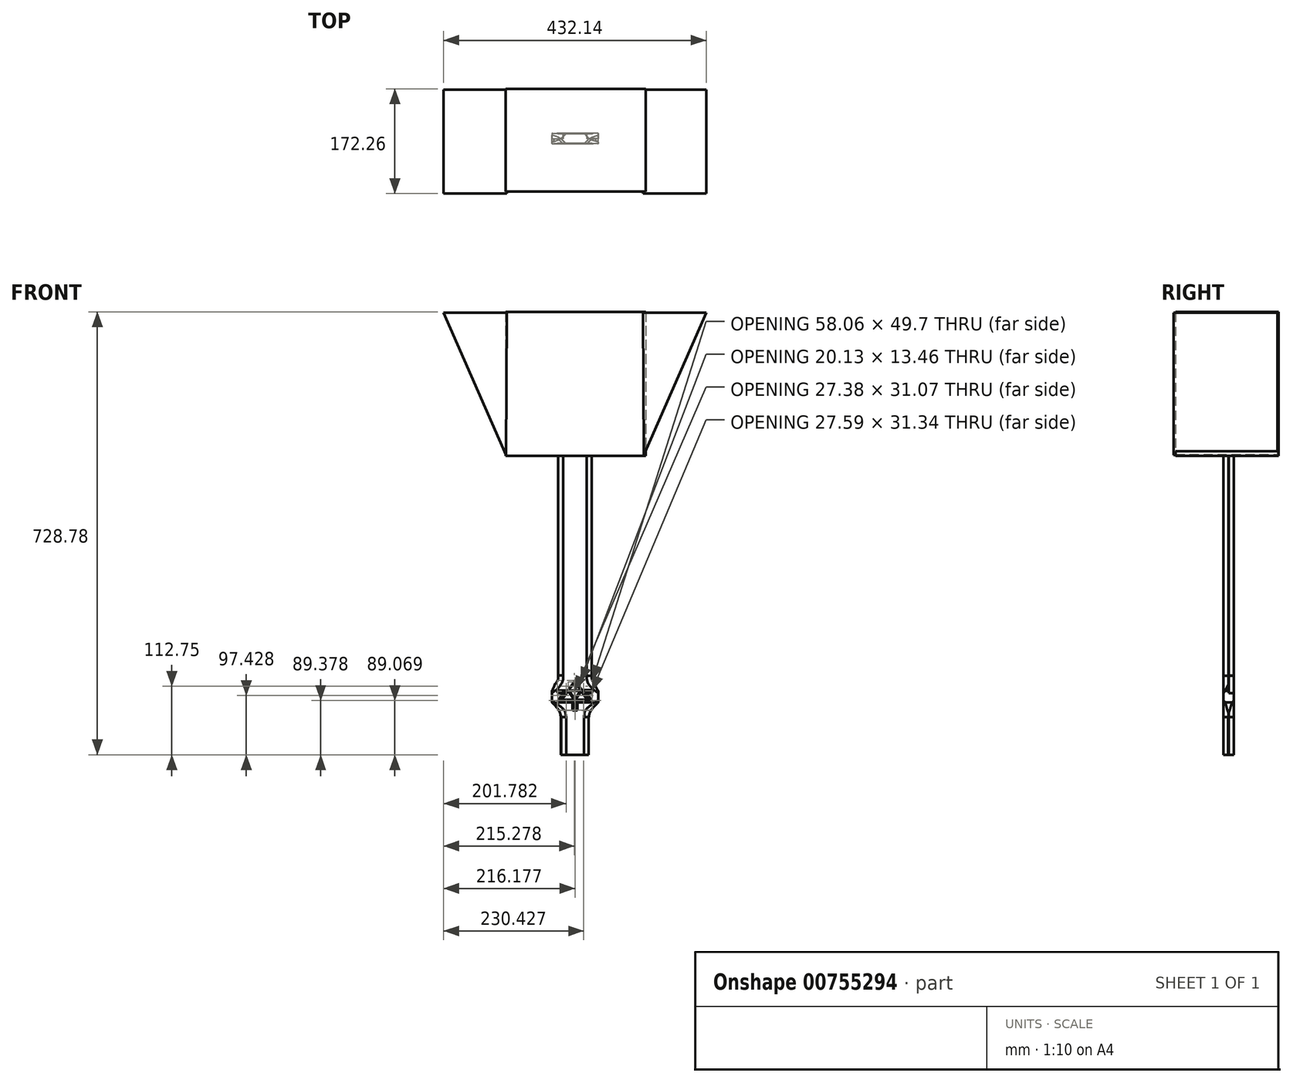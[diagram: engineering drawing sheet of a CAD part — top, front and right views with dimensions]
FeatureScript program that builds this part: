
annotation { "Feature Type Name" : "Feature", "Feature Type Description" : "" }
export const myFeature = defineFeature(function(context is Context, id is Id, definition is map)
    precondition{}
    {
        {
            var Q0;
            Q0=qCreatedBy(makeId("Front.planeOp"),FACE);
            var sketch = newSketch(context, id + "F0", { "sketchPlane" : qUnion([Q0])});
            skLineSegment(sketch, "E0", {"start": v(-23.18, 89.36) * mm, "end": v(-23.18, 27.94) * mm});
            skLineSegment(sketch, "E1", {"start": v(-23.18, 27.94) * mm, "end": v(22.75, 27.94) * mm});
            skLineSegment(sketch, "E2", {"start": v(22.75, 27.94) * mm, "end": v(22.75, 89.36) * mm});
            skFitSpline(sketch, "E3", {"points": [v(-23.18, 89.36) * mm, v(-25.2, 98.78) * mm, v(-29.58, 105.34) * mm, v(-34.12, 110.56) * mm, v(-37.82, 114.26) * mm], "startDerivative": vector(-4.45, 34.79) * mm, "endDerivative": vector(-17.26, 16.67) * mm});
            skFitSpline(sketch, "E4", {"points": [v(22.75, 89.36) * mm, v(24.94, 98.27) * mm, v(29.82, 105.5) * mm, v(34.53, 110.56) * mm, v(38.16, 114.22) * mm], "startDerivative": vector(5.26, 33.12) * mm, "endDerivative": vector(16.94, 16.97) * mm});
            skLineSegment(sketch, "E5", {"start": v(-37.82, 114.26) * mm, "end": v(-37.82, 132.92) * mm});
            skLineSegment(sketch, "E6", {"start": v(38.16, 114.22) * mm, "end": v(38.16, 132.92) * mm});
            skFitSpline(sketch, "E7", {"points": [v(-37.82, 132.92) * mm, v(-34.87, 138.92) * mm, v(-32.96, 144.16) * mm, v(-31.8, 152.09) * mm, v(-31.68, 159) * mm], "startDerivative": vector(12.58, 24.9) * mm, "endDerivative": vector(-0.2, 26.4) * mm});
            skFitSpline(sketch, "E8", {"points": [v(38.16, 132.92) * mm, v(35.43, 137.9) * mm, v(32.87, 144.8) * mm, v(31.98, 152.47) * mm, v(31.85, 157.97) * mm], "startDerivative": vector(-11.86, 20.42) * mm, "endDerivative": vector(-0.27, 22.84) * mm});
            skLineSegment(sketch, "E9", {"start": v(-31.68, 159) * mm, "end": v(-31.68, 655.53) * mm});
            skLineSegment(sketch, "E10", {"start": v(31.85, 157.97) * mm, "end": v(31.87, 655.53) * mm});
            skFitSpline(sketch, "E11", {"points": [v(0, 770.67) * mm, v(5.75, 755.45) * mm, v(13.9, 732.8) * mm, v(20.44, 712.09) * mm, v(27.87, 687.66) * mm, v(30.7, 671.38) * mm, v(31.87, 655.53) * mm], "startDerivative": vector(35.97, -94.67) * mm, "endDerivative": vector(6.36, -107.63) * mm});
            skFitSpline(sketch, "E12", {"points": [v(0, 770.67) * mm, v(-7.17, 751.02) * mm, v(-17.08, 723.77) * mm, v(-25.22, 697.22) * mm, v(-28.94, 682) * mm, v(-31.68, 655.53) * mm], "startDerivative": vector(-36.3, -100.65) * mm, "endDerivative": vector(-10.82, -136.16) * mm});
            skSolve(sketch);
        }
        {
            var Q0;
            Q0=makeQuery(id+"F0.imprint","IMPRINT",FACE,{"disambiguationData":[TD([[makeQuery(id+"F0.imprint","IMPRINT",EDGE,{"derivedFrom":sQuery(id+"F0.wireOp",EDGE,"E0")}),1.0]])]});
            extrude(context, id + "F1", {"entities" : qUnion([Q0]), "depth" : 0.25 * mm, "offsetDistance" : 25.4 * mm});
        }
        {
            var Q0;
            Q0=makeQuery(id+"F1.opExtrude","CAP_FACE",FACE,{"disambiguationData":[OSD([sQuery(id+"F0.wireOp",EDGE,"E0"),sQuery(id+"F0.wireOp",EDGE,"E1"),sQuery(id+"F0.wireOp",EDGE,"E2"),sQuery(id+"F0.wireOp",EDGE,"E3"),sQuery(id+"F0.wireOp",EDGE,"E4"),sQuery(id+"F0.wireOp",EDGE,"E5"),sQuery(id+"F0.wireOp",EDGE,"E6"),sQuery(id+"F0.wireOp",EDGE,"E7"),sQuery(id+"F0.wireOp",EDGE,"E8"),sQuery(id+"F0.wireOp",EDGE,"E9"),sQuery(id+"F0.wireOp",EDGE,"E10"),sQuery(id+"F0.wireOp",EDGE,"E11"),sQuery(id+"F0.wireOp",EDGE,"E12")])],"isStart":true});
            extrude(context, id + "F2", {"entities" : qUnion([Q0]), "operationType" : NewBodyOperationType.ADD, "depth" : 0.25 * mm, "offsetDistance" : 25.4 * mm});
        }
        {
            var Q0;
            Q0=makeQuery(id+"F2.opExtrude","CAP_FACE",FACE,{"disambiguationData":[OSD([sQuery(id+"F0.wireOp",EDGE,"E0"),sQuery(id+"F0.wireOp",EDGE,"E1"),sQuery(id+"F0.wireOp",EDGE,"E2"),sQuery(id+"F0.wireOp",EDGE,"E3"),sQuery(id+"F0.wireOp",EDGE,"E4"),sQuery(id+"F0.wireOp",EDGE,"E5"),sQuery(id+"F0.wireOp",EDGE,"E6"),sQuery(id+"F0.wireOp",EDGE,"E7"),sQuery(id+"F0.wireOp",EDGE,"E8"),sQuery(id+"F0.wireOp",EDGE,"E9"),sQuery(id+"F0.wireOp",EDGE,"E10"),sQuery(id+"F0.wireOp",EDGE,"E11"),sQuery(id+"F0.wireOp",EDGE,"E12")])],"isStart":false});
            var sketch = newSketch(context, id + "F3", { "sketchPlane" : qUnion([Q0])});
            skLineSegment(sketch, "E13", {"start": v(-14.88, 27.94) * mm, "end": v(-14.88, 90.23) * mm});
            skFitSpline(sketch, "E14", {"points": [v(-14.88, 90.23) * mm, v(-16.73, 99.87) * mm, v(-22.43, 106.47) * mm, v(-31.13, 113.07) * mm, v(-38.16, 117.57) * mm], "startDerivative": vector(-3.35, 40.52) * mm, "endDerivative": vector(-28.93, 17.8) * mm});
            skLineSegment(sketch, "E15", {"start": v(14.47, 27.94) * mm, "end": v(14.47, 90.23) * mm});
            skFitSpline(sketch, "E16", {"points": [v(14.47, 90.23) * mm, v(16.95, 99.87) * mm, v(22.69, 106.47) * mm, v(31.86, 113.07) * mm, v(37.82, 117.57) * mm], "startDerivative": vector(6.55, 39.9) * mm, "endDerivative": vector(24.56, 19.23) * mm});
            skFitSpline(sketch, "E17", {"points": [v(37.82, 129.66) * mm, v(28.49, 136.84) * mm, v(22.69, 144.12) * mm, v(19.73, 151.4) * mm, v(19.42, 158.88) * mm], "startDerivative": vector(-34.92, 24.3) * mm, "endDerivative": vector(1.06, 33.21) * mm});
            skFitSpline(sketch, "E18", {"points": [v(-38.16, 129.14) * mm, v(-30.17, 135.78) * mm, v(-23.73, 142.32) * mm, v(-20.88, 147.8) * mm, v(-19.51, 153.3) * mm, v(-19.62, 158.04) * mm], "startDerivative": vector(33.35, 27.05) * mm, "endDerivative": vector(-2.46, 28.44) * mm});
            skLineSegment(sketch, "E19", {"start": v(-19.62, 158.04) * mm, "end": v(-19.62, 652.03) * mm});
            skLineSegment(sketch, "E20", {"start": v(19.42, 158.88) * mm, "end": v(19.33, 652.03) * mm});
            skFitSpline(sketch, "E21", {"points": [v(19.33, 652.03) * mm, v(15.9, 673.87) * mm, v(8.12, 693.88) * mm, v(0, 711.54) * mm], "startDerivative": vector(-6.72, 64.73) * mm, "endDerivative": vector(-25.08, 54.21) * mm});
            skFitSpline(sketch, "E22", {"points": [v(-19.62, 652.03) * mm, v(-16.6, 673.4) * mm, v(-8.12, 694.59) * mm, v(0, 711.54) * mm], "startDerivative": vector(4.95, 63.37) * mm, "endDerivative": vector(25.12, 52.1) * mm});
            skSolve(sketch);
        }
        {
            var Q0;
            {var subQ4=sQuery(id+"F3.wireOp",EDGE,"E13");Q0=makeQuery(id+"F3.imprint","IMPRINT",FACE,{"disambiguationData":[TD([[makeQuery(id+"F3.imprint","IMPRINT",EDGE,{"derivedFrom":subQ4}),-1.0]])]});}
            extrude(context, id + "F4", {"entities" : qUnion([Q0]), "operationType" : NewBodyOperationType.ADD, "depth" : 12.7 * mm, "offsetDistance" : 25.4 * mm});
        }
        {
            var Q0;
            Q0=makeQuery(id+"F4.opExtrude","CAP_FACE",FACE,{"disambiguationData":[OSD([sQuery(id+"F0.wireOp",EDGE,"E1"),sQuery(id+"F0.wireOp",EDGE,"E5"),sQuery(id+"F0.wireOp",EDGE,"E6"),sQuery(id+"F3.wireOp",EDGE,"E13"),sQuery(id+"F3.wireOp",EDGE,"E14"),sQuery(id+"F3.wireOp",EDGE,"E15"),sQuery(id+"F3.wireOp",EDGE,"E16"),sQuery(id+"F3.wireOp",EDGE,"E17"),sQuery(id+"F3.wireOp",EDGE,"E18"),sQuery(id+"F3.wireOp",EDGE,"E19"),sQuery(id+"F3.wireOp",EDGE,"E20"),sQuery(id+"F3.wireOp",EDGE,"E21"),sQuery(id+"F3.wireOp",EDGE,"E22")])],"isStart":false});
            extrude(context, id + "F5", {"entities" : qUnion([Q0]), "operationType" : NewBodyOperationType.ADD, "oppositeDirection" : true, "depth" : 25.9 * mm, "offsetDistance" : 25.4 * mm});
        }
        {
            var Q0;
            Q0=makeQuery(id+"F4.opExtrude","CAP_EDGE",EDGE,{"disambiguationData":[OSD([sQuery(id+"F3.wireOp",EDGE,"E22")])],"isStart":true});
            var Q1;
            Q1=makeQuery(id+"F4.opExtrude","CAP_EDGE",EDGE,{"disambiguationData":[OSD([sQuery(id+"F3.wireOp",EDGE,"E19")])],"isStart":true});
            var Q2;
            Q2=makeQuery(id+"F4.opExtrude","CAP_EDGE",EDGE,{"disambiguationData":[OSD([sQuery(id+"F3.wireOp",EDGE,"E21")])],"isStart":true});
            var Q3;
            Q3=makeQuery(id+"F4.opExtrude","CAP_EDGE",EDGE,{"disambiguationData":[OSD([sQuery(id+"F3.wireOp",EDGE,"E20")])],"isStart":true});
            var Q4;
            Q4=makeQuery(id+"F4.opExtrude","CAP_EDGE",EDGE,{"disambiguationData":[OSD([sQuery(id+"F3.wireOp",EDGE,"E17")])],"isStart":true});
            var Q5;
            Q5=makeQuery(id+"F4.opExtrude","CAP_EDGE",EDGE,{"disambiguationData":[OSD([sQuery(id+"F3.wireOp",EDGE,"E18")])],"isStart":true});
            var Q6;
            Q6=makeQuery(id+"F4.opExtrude","CAP_EDGE",EDGE,{"disambiguationData":[OSD([sQuery(id+"F3.wireOp",EDGE,"E14")])],"isStart":true});
            var Q7;
            Q7=makeQuery(id+"F4.opExtrude","CAP_EDGE",EDGE,{"disambiguationData":[OSD([sQuery(id+"F3.wireOp",EDGE,"E16")])],"isStart":true});
            var Q8;
            Q8=makeQuery(id+"F4.opExtrude","CAP_EDGE",EDGE,{"disambiguationData":[OSD([sQuery(id+"F3.wireOp",EDGE,"E15")])],"isStart":true});
            var Q9;
            Q9=makeQuery(id+"F4.opExtrude","CAP_EDGE",EDGE,{"disambiguationData":[OSD([sQuery(id+"F3.wireOp",EDGE,"E13")])],"isStart":true});
            chamfer(context, id + "F6", {"entities" : qUnion([Q0, Q1, Q2, Q3, Q4, Q5, Q6, Q7, Q8, Q9]), "chamferType" : ChamferType.OFFSET_ANGLE, "width" : 8.13 * mm, "oppositeDirection" : false, "angle" : 47 * degree, "tangentPropagation" : true});
        }
        {
            var Q0;
            Q0=makeQuery(id+"F5.boolean.opBoolean","INTERSECT",EDGE,{"derivedFrom":[makeQuery(id+"F1.opExtrude","CAP_FACE",FACE,{"disambiguationData":[OSD([sQuery(id+"F0.wireOp",EDGE,"E0"),sQuery(id+"F0.wireOp",EDGE,"E1"),sQuery(id+"F0.wireOp",EDGE,"E2"),sQuery(id+"F0.wireOp",EDGE,"E3"),sQuery(id+"F0.wireOp",EDGE,"E4"),sQuery(id+"F0.wireOp",EDGE,"E5"),sQuery(id+"F0.wireOp",EDGE,"E6"),sQuery(id+"F0.wireOp",EDGE,"E7"),sQuery(id+"F0.wireOp",EDGE,"E8"),sQuery(id+"F0.wireOp",EDGE,"E9"),sQuery(id+"F0.wireOp",EDGE,"E10"),sQuery(id+"F0.wireOp",EDGE,"E11"),sQuery(id+"F0.wireOp",EDGE,"E12")])],"isStart":false}),makeQuery(id+"F5.opExtrude","SWEPT_FACE",FACE,{"disambiguationData":[OSD([sQuery(id+"F3.wireOp",EDGE,"E20")])]})]});
            var Q1;
            Q1=makeQuery(id+"F5.boolean.opBoolean","INTERSECT",EDGE,{"derivedFrom":[makeQuery(id+"F1.opExtrude","CAP_FACE",FACE,{"disambiguationData":[OSD([sQuery(id+"F0.wireOp",EDGE,"E0"),sQuery(id+"F0.wireOp",EDGE,"E1"),sQuery(id+"F0.wireOp",EDGE,"E2"),sQuery(id+"F0.wireOp",EDGE,"E3"),sQuery(id+"F0.wireOp",EDGE,"E4"),sQuery(id+"F0.wireOp",EDGE,"E5"),sQuery(id+"F0.wireOp",EDGE,"E6"),sQuery(id+"F0.wireOp",EDGE,"E7"),sQuery(id+"F0.wireOp",EDGE,"E8"),sQuery(id+"F0.wireOp",EDGE,"E9"),sQuery(id+"F0.wireOp",EDGE,"E10"),sQuery(id+"F0.wireOp",EDGE,"E11"),sQuery(id+"F0.wireOp",EDGE,"E12")])],"isStart":false}),makeQuery(id+"F5.opExtrude","SWEPT_FACE",FACE,{"disambiguationData":[OSD([sQuery(id+"F3.wireOp",EDGE,"E17")])]})]});
            var Q2;
            Q2=makeQuery(id+"F5.boolean.opBoolean","INTERSECT",EDGE,{"derivedFrom":[makeQuery(id+"F1.opExtrude","CAP_FACE",FACE,{"disambiguationData":[OSD([sQuery(id+"F0.wireOp",EDGE,"E0"),sQuery(id+"F0.wireOp",EDGE,"E1"),sQuery(id+"F0.wireOp",EDGE,"E2"),sQuery(id+"F0.wireOp",EDGE,"E3"),sQuery(id+"F0.wireOp",EDGE,"E4"),sQuery(id+"F0.wireOp",EDGE,"E5"),sQuery(id+"F0.wireOp",EDGE,"E6"),sQuery(id+"F0.wireOp",EDGE,"E7"),sQuery(id+"F0.wireOp",EDGE,"E8"),sQuery(id+"F0.wireOp",EDGE,"E9"),sQuery(id+"F0.wireOp",EDGE,"E10"),sQuery(id+"F0.wireOp",EDGE,"E11"),sQuery(id+"F0.wireOp",EDGE,"E12")])],"isStart":false}),makeQuery(id+"F5.opExtrude","SWEPT_FACE",FACE,{"disambiguationData":[OSD([sQuery(id+"F3.wireOp",EDGE,"E16")])]})]});
            var Q3;
            Q3=makeQuery(id+"F5.boolean.opBoolean","INTERSECT",EDGE,{"derivedFrom":[makeQuery(id+"F1.opExtrude","CAP_FACE",FACE,{"disambiguationData":[OSD([sQuery(id+"F0.wireOp",EDGE,"E0"),sQuery(id+"F0.wireOp",EDGE,"E1"),sQuery(id+"F0.wireOp",EDGE,"E2"),sQuery(id+"F0.wireOp",EDGE,"E3"),sQuery(id+"F0.wireOp",EDGE,"E4"),sQuery(id+"F0.wireOp",EDGE,"E5"),sQuery(id+"F0.wireOp",EDGE,"E6"),sQuery(id+"F0.wireOp",EDGE,"E7"),sQuery(id+"F0.wireOp",EDGE,"E8"),sQuery(id+"F0.wireOp",EDGE,"E9"),sQuery(id+"F0.wireOp",EDGE,"E10"),sQuery(id+"F0.wireOp",EDGE,"E11"),sQuery(id+"F0.wireOp",EDGE,"E12")])],"isStart":false}),makeQuery(id+"F5.opExtrude","SWEPT_FACE",FACE,{"disambiguationData":[OSD([sQuery(id+"F3.wireOp",EDGE,"E15")])]})]});
            var Q4;
            Q4=makeQuery(id+"F5.boolean.opBoolean","INTERSECT",EDGE,{"derivedFrom":[makeQuery(id+"F1.opExtrude","CAP_FACE",FACE,{"disambiguationData":[OSD([sQuery(id+"F0.wireOp",EDGE,"E0"),sQuery(id+"F0.wireOp",EDGE,"E1"),sQuery(id+"F0.wireOp",EDGE,"E2"),sQuery(id+"F0.wireOp",EDGE,"E3"),sQuery(id+"F0.wireOp",EDGE,"E4"),sQuery(id+"F0.wireOp",EDGE,"E5"),sQuery(id+"F0.wireOp",EDGE,"E6"),sQuery(id+"F0.wireOp",EDGE,"E7"),sQuery(id+"F0.wireOp",EDGE,"E8"),sQuery(id+"F0.wireOp",EDGE,"E9"),sQuery(id+"F0.wireOp",EDGE,"E10"),sQuery(id+"F0.wireOp",EDGE,"E11"),sQuery(id+"F0.wireOp",EDGE,"E12")])],"isStart":false}),makeQuery(id+"F5.opExtrude","SWEPT_FACE",FACE,{"disambiguationData":[OSD([sQuery(id+"F3.wireOp",EDGE,"E13")])]})]});
            var Q5;
            Q5=makeQuery(id+"F5.boolean.opBoolean","INTERSECT",EDGE,{"derivedFrom":[makeQuery(id+"F1.opExtrude","CAP_FACE",FACE,{"disambiguationData":[OSD([sQuery(id+"F0.wireOp",EDGE,"E0"),sQuery(id+"F0.wireOp",EDGE,"E1"),sQuery(id+"F0.wireOp",EDGE,"E2"),sQuery(id+"F0.wireOp",EDGE,"E3"),sQuery(id+"F0.wireOp",EDGE,"E4"),sQuery(id+"F0.wireOp",EDGE,"E5"),sQuery(id+"F0.wireOp",EDGE,"E6"),sQuery(id+"F0.wireOp",EDGE,"E7"),sQuery(id+"F0.wireOp",EDGE,"E8"),sQuery(id+"F0.wireOp",EDGE,"E9"),sQuery(id+"F0.wireOp",EDGE,"E10"),sQuery(id+"F0.wireOp",EDGE,"E11"),sQuery(id+"F0.wireOp",EDGE,"E12")])],"isStart":false}),makeQuery(id+"F5.opExtrude","SWEPT_FACE",FACE,{"disambiguationData":[OSD([sQuery(id+"F3.wireOp",EDGE,"E14")])]})]});
            var Q6;
            Q6=makeQuery(id+"F5.boolean.opBoolean","INTERSECT",EDGE,{"derivedFrom":[makeQuery(id+"F1.opExtrude","CAP_FACE",FACE,{"disambiguationData":[OSD([sQuery(id+"F0.wireOp",EDGE,"E0"),sQuery(id+"F0.wireOp",EDGE,"E1"),sQuery(id+"F0.wireOp",EDGE,"E2"),sQuery(id+"F0.wireOp",EDGE,"E3"),sQuery(id+"F0.wireOp",EDGE,"E4"),sQuery(id+"F0.wireOp",EDGE,"E5"),sQuery(id+"F0.wireOp",EDGE,"E6"),sQuery(id+"F0.wireOp",EDGE,"E7"),sQuery(id+"F0.wireOp",EDGE,"E8"),sQuery(id+"F0.wireOp",EDGE,"E9"),sQuery(id+"F0.wireOp",EDGE,"E10"),sQuery(id+"F0.wireOp",EDGE,"E11"),sQuery(id+"F0.wireOp",EDGE,"E12")])],"isStart":false}),makeQuery(id+"F5.opExtrude","SWEPT_FACE",FACE,{"disambiguationData":[OSD([sQuery(id+"F3.wireOp",EDGE,"E18")])]})]});
            var Q7;
            Q7=makeQuery(id+"F5.boolean.opBoolean","INTERSECT",EDGE,{"derivedFrom":[makeQuery(id+"F1.opExtrude","CAP_FACE",FACE,{"disambiguationData":[OSD([sQuery(id+"F0.wireOp",EDGE,"E0"),sQuery(id+"F0.wireOp",EDGE,"E1"),sQuery(id+"F0.wireOp",EDGE,"E2"),sQuery(id+"F0.wireOp",EDGE,"E3"),sQuery(id+"F0.wireOp",EDGE,"E4"),sQuery(id+"F0.wireOp",EDGE,"E5"),sQuery(id+"F0.wireOp",EDGE,"E6"),sQuery(id+"F0.wireOp",EDGE,"E7"),sQuery(id+"F0.wireOp",EDGE,"E8"),sQuery(id+"F0.wireOp",EDGE,"E9"),sQuery(id+"F0.wireOp",EDGE,"E10"),sQuery(id+"F0.wireOp",EDGE,"E11"),sQuery(id+"F0.wireOp",EDGE,"E12")])],"isStart":false}),makeQuery(id+"F5.opExtrude","SWEPT_FACE",FACE,{"disambiguationData":[OSD([sQuery(id+"F3.wireOp",EDGE,"E19")])]})]});
            var Q8;
            Q8=makeQuery(id+"F5.boolean.opBoolean","INTERSECT",EDGE,{"derivedFrom":[makeQuery(id+"F1.opExtrude","CAP_FACE",FACE,{"disambiguationData":[OSD([sQuery(id+"F0.wireOp",EDGE,"E0"),sQuery(id+"F0.wireOp",EDGE,"E1"),sQuery(id+"F0.wireOp",EDGE,"E2"),sQuery(id+"F0.wireOp",EDGE,"E3"),sQuery(id+"F0.wireOp",EDGE,"E4"),sQuery(id+"F0.wireOp",EDGE,"E5"),sQuery(id+"F0.wireOp",EDGE,"E6"),sQuery(id+"F0.wireOp",EDGE,"E7"),sQuery(id+"F0.wireOp",EDGE,"E8"),sQuery(id+"F0.wireOp",EDGE,"E9"),sQuery(id+"F0.wireOp",EDGE,"E10"),sQuery(id+"F0.wireOp",EDGE,"E11"),sQuery(id+"F0.wireOp",EDGE,"E12")])],"isStart":false}),makeQuery(id+"F5.opExtrude","SWEPT_FACE",FACE,{"disambiguationData":[OSD([sQuery(id+"F3.wireOp",EDGE,"E22")])]})]});
            var Q9;
            Q9=makeQuery(id+"F5.boolean.opBoolean","INTERSECT",EDGE,{"derivedFrom":[makeQuery(id+"F1.opExtrude","CAP_FACE",FACE,{"disambiguationData":[OSD([sQuery(id+"F0.wireOp",EDGE,"E0"),sQuery(id+"F0.wireOp",EDGE,"E1"),sQuery(id+"F0.wireOp",EDGE,"E2"),sQuery(id+"F0.wireOp",EDGE,"E3"),sQuery(id+"F0.wireOp",EDGE,"E4"),sQuery(id+"F0.wireOp",EDGE,"E5"),sQuery(id+"F0.wireOp",EDGE,"E6"),sQuery(id+"F0.wireOp",EDGE,"E7"),sQuery(id+"F0.wireOp",EDGE,"E8"),sQuery(id+"F0.wireOp",EDGE,"E9"),sQuery(id+"F0.wireOp",EDGE,"E10"),sQuery(id+"F0.wireOp",EDGE,"E11"),sQuery(id+"F0.wireOp",EDGE,"E12")])],"isStart":false}),makeQuery(id+"F5.opExtrude","SWEPT_FACE",FACE,{"disambiguationData":[OSD([sQuery(id+"F3.wireOp",EDGE,"E21")])]})]});
            chamfer(context, id + "F7", {"entities" : qUnion([Q0, Q1, Q2, Q3, Q4, Q5, Q6, Q7, Q8, Q9]), "width" : 8.13 * mm, "tangentPropagation" : true});
        }
        {
            var Q0;
            Q0=makeQuery(id+"F5.opExtrude","CAP_FACE",FACE,{"disambiguationData":[OSD([sQuery(id+"F0.wireOp",EDGE,"E1"),sQuery(id+"F0.wireOp",EDGE,"E5"),sQuery(id+"F0.wireOp",EDGE,"E6"),sQuery(id+"F3.wireOp",EDGE,"E13"),sQuery(id+"F3.wireOp",EDGE,"E14"),sQuery(id+"F3.wireOp",EDGE,"E15"),sQuery(id+"F3.wireOp",EDGE,"E16"),sQuery(id+"F3.wireOp",EDGE,"E17"),sQuery(id+"F3.wireOp",EDGE,"E18"),sQuery(id+"F3.wireOp",EDGE,"E19"),sQuery(id+"F3.wireOp",EDGE,"E20"),sQuery(id+"F3.wireOp",EDGE,"E21"),sQuery(id+"F3.wireOp",EDGE,"E22")])],"isStart":false});
            extrude(context, id + "F8", {"entities" : qUnion([Q0]), "operationType" : NewBodyOperationType.REMOVE, "oppositeDirection" : true, "depth" : 5.33 * mm, "offsetDistance" : 25.4 * mm});
        }
        {
            var Q0;
            Q0=makeQuery(id+"F4.opExtrude","CAP_FACE",FACE,{"disambiguationData":[OSD([sQuery(id+"F0.wireOp",EDGE,"E1"),sQuery(id+"F0.wireOp",EDGE,"E5"),sQuery(id+"F0.wireOp",EDGE,"E6"),sQuery(id+"F3.wireOp",EDGE,"E13"),sQuery(id+"F3.wireOp",EDGE,"E14"),sQuery(id+"F3.wireOp",EDGE,"E15"),sQuery(id+"F3.wireOp",EDGE,"E16"),sQuery(id+"F3.wireOp",EDGE,"E17"),sQuery(id+"F3.wireOp",EDGE,"E18"),sQuery(id+"F3.wireOp",EDGE,"E19"),sQuery(id+"F3.wireOp",EDGE,"E20"),sQuery(id+"F3.wireOp",EDGE,"E21"),sQuery(id+"F3.wireOp",EDGE,"E22")])],"isStart":false});
            extrude(context, id + "F9", {"entities" : qUnion([Q0]), "operationType" : NewBodyOperationType.REMOVE, "oppositeDirection" : true, "depth" : 4 * mm, "offsetDistance" : 25.4 * mm});
        }
        {
            var Q0;
            {var subQ0=sQuery(id+"F0.wireOp",EDGE,"E12");var subQ1=sQuery(id+"F0.wireOp",EDGE,"E11");var subQ2=sQuery(id+"F0.wireOp",EDGE,"E10");var subQ3=sQuery(id+"F0.wireOp",EDGE,"E9");var subQ4=sQuery(id+"F0.wireOp",EDGE,"E8");var subQ5=sQuery(id+"F0.wireOp",EDGE,"E7");var subQ6=sQuery(id+"F0.wireOp",EDGE,"E6");var subQ7=sQuery(id+"F0.wireOp",EDGE,"E5");Q0=makeQuery(id+"F5.boolean.opBoolean","SPLIT",FACE,{"disambiguationData":[TD([makeQuery(id+"F1.opExtrude","SWEPT_FACE",FACE,{"disambiguationData":[OSD([subQ5])]})])],"derivedFrom":makeQuery(id+"F1.opExtrude","CAP_FACE",FACE,{"disambiguationData":[OSD([sQuery(id+"F0.wireOp",EDGE,"E0"),sQuery(id+"F0.wireOp",EDGE,"E1"),sQuery(id+"F0.wireOp",EDGE,"E2"),sQuery(id+"F0.wireOp",EDGE,"E3"),sQuery(id+"F0.wireOp",EDGE,"E4"),subQ7,subQ6,subQ5,subQ4,subQ3,subQ2,subQ1,subQ0])],"isStart":false})});}
            extrude(context, id + "F10", {"entities" : qUnion([Q0]), "operationType" : NewBodyOperationType.REMOVE, "oppositeDirection" : true, "depth" : 25.4 * mm, "offsetDistance" : 25.4 * mm});
        }
        {
            var Q0;
            Q0=makeQuery(id+"F8.boolean.opBoolean","COPY",FACE,{"derivedFrom":makeQuery(id+"F8.opExtrude","CAP_FACE",FACE,{"disambiguationData":[OSD([sQuery(id+"F0.wireOp",EDGE,"E1"),sQuery(id+"F0.wireOp",EDGE,"E5"),sQuery(id+"F0.wireOp",EDGE,"E6"),sQuery(id+"F3.wireOp",EDGE,"E13"),sQuery(id+"F3.wireOp",EDGE,"E14"),sQuery(id+"F3.wireOp",EDGE,"E15"),sQuery(id+"F3.wireOp",EDGE,"E16"),sQuery(id+"F3.wireOp",EDGE,"E17"),sQuery(id+"F3.wireOp",EDGE,"E18"),sQuery(id+"F3.wireOp",EDGE,"E19"),sQuery(id+"F3.wireOp",EDGE,"E20"),sQuery(id+"F3.wireOp",EDGE,"E21"),sQuery(id+"F3.wireOp",EDGE,"E22")])],"isStart":false})});
            extrude(context, id + "F11", {"entities" : qUnion([Q0]), "operationType" : NewBodyOperationType.ADD, "depth" : 0.76 * mm, "offsetDistance" : 25.4 * mm});
        }
        {
            var Q0;
            Q0=makeQuery(id+"F9.boolean.opBoolean","COPY",FACE,{"derivedFrom":makeQuery(id+"F9.opExtrude","CAP_FACE",FACE,{"disambiguationData":[OSD([sQuery(id+"F0.wireOp",EDGE,"E1"),sQuery(id+"F0.wireOp",EDGE,"E5"),sQuery(id+"F0.wireOp",EDGE,"E6"),sQuery(id+"F3.wireOp",EDGE,"E13"),sQuery(id+"F3.wireOp",EDGE,"E14"),sQuery(id+"F3.wireOp",EDGE,"E15"),sQuery(id+"F3.wireOp",EDGE,"E16"),sQuery(id+"F3.wireOp",EDGE,"E17"),sQuery(id+"F3.wireOp",EDGE,"E18"),sQuery(id+"F3.wireOp",EDGE,"E19"),sQuery(id+"F3.wireOp",EDGE,"E20"),sQuery(id+"F3.wireOp",EDGE,"E21"),sQuery(id+"F3.wireOp",EDGE,"E22")])],"isStart":false})});
            var sketch = newSketch(context, id + "F12", { "sketchPlane" : qUnion([Q0])});
            skLineSegment(sketch, "E23", {"start": v(-11.79, 134.23) * mm, "end": v(0, 150.22) * mm});
            skLineSegment(sketch, "E24", {"start": v(0, 150.22) * mm, "end": v(12.06, 133.96) * mm});
            skLineSegment(sketch, "E25", {"start": v(12.06, 133.96) * mm, "end": v(26.89, 133.96) * mm});
            skLineSegment(sketch, "E26", {"start": v(26.89, 129.23) * mm, "end": v(19.36, 129.23) * mm});
            skLineSegment(sketch, "E27", {"start": v(19.36, 129.23) * mm, "end": v(27.93, 116.9) * mm});
            skLineSegment(sketch, "E28", {"start": v(26.89, 114) * mm, "end": v(4.81, 114) * mm});
            skLineSegment(sketch, "E29", {"start": v(-5.35, 114) * mm, "end": v(-27.24, 114) * mm});
            skLineSegment(sketch, "E30", {"start": v(-27.9, 116.9) * mm, "end": v(-19.08, 129.43) * mm});
            skLineSegment(sketch, "E31", {"start": v(-19.08, 129.43) * mm, "end": v(-27.24, 129.43) * mm});
            skLineSegment(sketch, "E32", {"start": v(-11.79, 134.23) * mm, "end": v(-27.24, 134.23) * mm});
            skLineSegment(sketch, "E33", {"start": v(0, 147.42) * mm, "end": v(-9.27, 134.23) * mm});
            skLineSegment(sketch, "E34", {"start": v(-9.27, 134.23) * mm, "end": v(10.86, 133.96) * mm});
            skLineSegment(sketch, "E35", {"start": v(10.86, 133.96) * mm, "end": v(0, 147.42) * mm});
            skLineSegment(sketch, "E36", {"start": v(-11.79, 132.99) * mm, "end": v(-21.8, 119.4) * mm});
            skLineSegment(sketch, "E37", {"start": v(-21.25, 117.57) * mm, "end": v(-0.56, 117.57) * mm});
            skLineSegment(sketch, "E38", {"start": v(-0.56, 117.57) * mm, "end": v(-0.56, 102.3) * mm});
            skLineSegment(sketch, "E39", {"start": v(-4.22, 102.3) * mm, "end": v(-4.22, 113.14) * mm});
            skLineSegment(sketch, "E40", {"start": v(4.21, 113.14) * mm, "end": v(4.21, 102.3) * mm});
            skLineSegment(sketch, "E41", {"start": v(0.6, 102.3) * mm, "end": v(0.6, 117.57) * mm});
            skLineSegment(sketch, "E42", {"start": v(0.6, 117.57) * mm, "end": v(21.41, 117.57) * mm});
            skLineSegment(sketch, "E43", {"start": v(22.25, 118.83) * mm, "end": v(12.3, 132.54) * mm});
            skLineSegment(sketch, "E44", {"start": v(12.3, 132.54) * mm, "end": v(26.89, 132.54) * mm});
            skLineSegment(sketch, "E45", {"start": v(26.89, 130.12) * mm, "end": v(18.73, 130.12) * mm});
            skLineSegment(sketch, "E46", {"start": v(18.4, 128.97) * mm, "end": v(27.24, 116.24) * mm});
            skLineSegment(sketch, "E47", {"start": v(-20.22, 118.34) * mm, "end": v(-10.53, 132.13) * mm});
            skLineSegment(sketch, "E48", {"start": v(-10.53, 132.13) * mm, "end": v(-0.88, 118.24) * mm});
            skLineSegment(sketch, "E49", {"start": v(-0.88, 118.24) * mm, "end": v(-20.22, 118.34) * mm});
            skLineSegment(sketch, "E50", {"start": v(1.5, 118.34) * mm, "end": v(11.28, 132.25) * mm});
            skLineSegment(sketch, "E51", {"start": v(11.28, 132.25) * mm, "end": v(21.41, 118.34) * mm});
            skLineSegment(sketch, "E52", {"start": v(21.41, 118.34) * mm, "end": v(1.5, 118.34) * mm});
            skLineSegment(sketch, "E53", {"start": v(9.51, 132.94) * mm, "end": v(-9.05, 132.94) * mm});
            skLineSegment(sketch, "E54", {"start": v(-9.05, 132.94) * mm, "end": v(0, 119.04) * mm});
            skLineSegment(sketch, "E55", {"start": v(0, 119.04) * mm, "end": v(9.51, 132.94) * mm});
            skFitSpline(sketch, "E56", {"points": [v(-21.25, 117.57) * mm, v(-22.4, 117.93) * mm, v(-21.8, 119.4) * mm], "startDerivative": vector(-3.32, 0.3) * mm, "endDerivative": vector(2.1, 3.3) * mm});
            skFitSpline(sketch, "E57", {"points": [v(-27.24, 114) * mm, v(-28.28, 115.14) * mm, v(-27.9, 116.9) * mm], "startDerivative": vector(-2.88, 2.13) * mm, "endDerivative": vector(1.5, 3.64) * mm});
            skFitSpline(sketch, "E58", {"points": [v(-27.24, 129.43) * mm, v(-28.9, 130.86) * mm, v(-28.84, 133.23) * mm, v(-27.24, 134.23) * mm], "startDerivative": vector(-5.9, 3.35) * mm, "endDerivative": vector(6.04, 2.14) * mm});
            skFitSpline(sketch, "E59", {"points": [v(22.25, 118.83) * mm, v(22.47, 117.72) * mm, v(21.41, 117.57) * mm], "startDerivative": vector(1.1, -2.67) * mm, "endDerivative": vector(-2.78, 0.17) * mm});
            skLineSegment(sketch, "E60", {"start": v(-11.79, 132.99) * mm, "end": v(-27.37, 132.99) * mm});
            skLineSegment(sketch, "E61", {"start": v(26.7, 114.7) * mm, "end": v(4.81, 114.7) * mm});
            skLineSegment(sketch, "E62", {"start": v(3.19, 113.27) * mm, "end": v(3.38, 102.25) * mm});
            skLineSegment(sketch, "E63", {"start": v(-3, 102.25) * mm, "end": v(-3, 113.23) * mm});
            skLineSegment(sketch, "E64", {"start": v(-5.42, 115.26) * mm, "end": v(-26.92, 115.26) * mm});
            skLineSegment(sketch, "E65", {"start": v(-27.2, 116.42) * mm, "end": v(-18, 129.5) * mm});
            skLineSegment(sketch, "E66", {"start": v(-19.1, 130.43) * mm, "end": v(-27.37, 130.43) * mm});
            skFitSpline(sketch, "E67", {"points": [v(-27.37, 132.99) * mm, v(-28.15, 131.74) * mm, v(-27.37, 130.43) * mm], "startDerivative": vector(-2.36, -2.5) * mm, "endDerivative": vector(2.34, -2.6) * mm});
            skFitSpline(sketch, "E68", {"points": [v(26.89, 133.96) * mm, v(28.5, 132.99) * mm, v(28.73, 130.43) * mm, v(26.89, 129.23) * mm], "startDerivative": vector(5.97, -1.95) * mm, "endDerivative": vector(-6.8, -2.42) * mm});
            skFitSpline(sketch, "E69", {"points": [v(26.89, 130.12) * mm, v(27.98, 131.53) * mm, v(26.89, 132.54) * mm], "startDerivative": vector(3.22, 2.86) * mm, "endDerivative": vector(-3.32, 1.98) * mm});
            skFitSpline(sketch, "E70", {"points": [v(18.73, 130.12) * mm, v(18.23, 129.75) * mm, v(18.4, 128.97) * mm], "startDerivative": vector(-1.4, -0.61) * mm, "endDerivative": vector(0.7, -1.65) * mm});
            skFitSpline(sketch, "E71", {"points": [v(27.24, 116.24) * mm, v(27.43, 115.26) * mm, v(26.7, 114.7) * mm], "startDerivative": vector(0.84, -2.13) * mm, "endDerivative": vector(-1.93, -0.96) * mm});
            skFitSpline(sketch, "E72", {"points": [v(27.93, 116.9) * mm, v(28.3, 115.33) * mm, v(27.7, 114.19) * mm, v(26.89, 114) * mm], "startDerivative": vector(1.64, -4.12) * mm, "endDerivative": vector(-3.1, -0.07) * mm});
            skFitSpline(sketch, "E73", {"points": [v(4.81, 114.7) * mm, v(3.92, 114.6) * mm, v(3.37, 114.15) * mm, v(3.19, 113.27) * mm], "startDerivative": vector(-2.72, 0.02) * mm, "endDerivative": vector(-0.22, -2.76) * mm});
            skFitSpline(sketch, "E74", {"points": [v(4.81, 114) * mm, v(4.22, 113.8) * mm, v(4.21, 113.14) * mm], "startDerivative": vector(-1.5, -0.2) * mm, "endDerivative": vector(0.3, -1.52) * mm});
            skFitSpline(sketch, "E75", {"points": [v(4.21, 102.3) * mm, v(3.38, 100.95) * mm, v(1.67, 100.75) * mm, v(0, 101.38) * mm], "startDerivative": vector(-1.94, -4.96) * mm, "endDerivative": vector(-4.65, 2.26) * mm});
            skFitSpline(sketch, "E76", {"points": [v(0.6, 102.3) * mm, v(1.44, 101.61) * mm, v(2.73, 101.58) * mm, v(3.38, 102.25) * mm], "startDerivative": vector(2.16, -2.4) * mm, "endDerivative": vector(1.66, 2.62) * mm});
            skFitSpline(sketch, "E77", {"points": [v(-0.56, 102.3) * mm, v(-1.1, 101.78) * mm, v(-2.42, 101.75) * mm, v(-3, 102.25) * mm], "startDerivative": vector(-1.33, -2) * mm, "endDerivative": vector(-1.49, 1.96) * mm});
            skFitSpline(sketch, "E78", {"points": [v(0, 101.38) * mm, v(-0.56, 100.71) * mm, v(-3, 100.75) * mm, v(-4.22, 102.3) * mm], "startDerivative": vector(-1.43, -3.14) * mm, "endDerivative": vector(-2.38, 5.15) * mm});
            skFitSpline(sketch, "E79", {"points": [v(-3, 113.23) * mm, v(-3, 114.27) * mm, v(-4.01, 115.29) * mm, v(-5.42, 115.26) * mm], "startDerivative": vector(0.63, 3.44) * mm, "endDerivative": vector(-4.15, -0.82) * mm});
            skFitSpline(sketch, "E80", {"points": [v(-5.35, 114) * mm, v(-4.5, 114) * mm, v(-4.22, 113.14) * mm], "startDerivative": vector(2, 0.42) * mm, "endDerivative": vector(0.26, -2.12) * mm});
            skFitSpline(sketch, "E81", {"points": [v(-26.92, 115.26) * mm, v(-27.37, 115.58) * mm, v(-27.2, 116.42) * mm], "startDerivative": vector(-1.3, 0.54) * mm, "endDerivative": vector(0.67, 1.74) * mm});
            skFitSpline(sketch, "E82", {"points": [v(-19.1, 130.43) * mm, v(-18.31, 130.12) * mm, v(-18, 129.5) * mm], "startDerivative": vector(1.7, -0.42) * mm, "endDerivative": vector(0.44, -1.46) * mm});
            skSolve(sketch);
        }
        {
            var Q0;
            Q0=makeQuery(id+"F12.imprint","IMPRINT",FACE,{"disambiguationData":[TD([[makeQuery(id+"F12.imprint","IMPRINT",EDGE,{"derivedFrom":sQuery(id+"F12.wireOp",EDGE,"E23")}),-1.0]])]});
            extrude(context, id + "F13", {"entities" : qUnion([Q0]), "operationType" : NewBodyOperationType.ADD, "depth" : 12.7 * mm, "offsetDistance" : 25.4 * mm});
        }
        {
            var Q0;
            Q0=makeQuery(id+"F13.opExtrude","CAP_FACE",FACE,{"disambiguationData":[OSD([sQuery(id+"F12.wireOp",EDGE,"E23"),sQuery(id+"F12.wireOp",EDGE,"E24"),sQuery(id+"F12.wireOp",EDGE,"E25"),sQuery(id+"F12.wireOp",EDGE,"E26"),sQuery(id+"F12.wireOp",EDGE,"E27"),sQuery(id+"F12.wireOp",EDGE,"E28"),sQuery(id+"F12.wireOp",EDGE,"E29"),sQuery(id+"F12.wireOp",EDGE,"E30"),sQuery(id+"F12.wireOp",EDGE,"E31"),sQuery(id+"F12.wireOp",EDGE,"E32"),sQuery(id+"F12.wireOp",EDGE,"E33"),sQuery(id+"F12.wireOp",EDGE,"E34"),sQuery(id+"F12.wireOp",EDGE,"E35"),sQuery(id+"F12.wireOp",EDGE,"E36"),sQuery(id+"F12.wireOp",EDGE,"E37"),sQuery(id+"F12.wireOp",EDGE,"E38"),sQuery(id+"F12.wireOp",EDGE,"E39"),sQuery(id+"F12.wireOp",EDGE,"E40"),sQuery(id+"F12.wireOp",EDGE,"E41"),sQuery(id+"F12.wireOp",EDGE,"E42"),sQuery(id+"F12.wireOp",EDGE,"E43"),sQuery(id+"F12.wireOp",EDGE,"E44"),sQuery(id+"F12.wireOp",EDGE,"E45"),sQuery(id+"F12.wireOp",EDGE,"E46"),sQuery(id+"F12.wireOp",EDGE,"E47"),sQuery(id+"F12.wireOp",EDGE,"E48"),sQuery(id+"F12.wireOp",EDGE,"E49"),sQuery(id+"F12.wireOp",EDGE,"E50"),sQuery(id+"F12.wireOp",EDGE,"E51"),sQuery(id+"F12.wireOp",EDGE,"E52"),sQuery(id+"F12.wireOp",EDGE,"E53"),sQuery(id+"F12.wireOp",EDGE,"E54"),sQuery(id+"F12.wireOp",EDGE,"E55"),sQuery(id+"F12.wireOp",EDGE,"E56"),sQuery(id+"F12.wireOp",EDGE,"E57"),sQuery(id+"F12.wireOp",EDGE,"E58"),sQuery(id+"F12.wireOp",EDGE,"E59"),sQuery(id+"F12.wireOp",EDGE,"E60"),sQuery(id+"F12.wireOp",EDGE,"E61"),sQuery(id+"F12.wireOp",EDGE,"E62"),sQuery(id+"F12.wireOp",EDGE,"E63"),sQuery(id+"F12.wireOp",EDGE,"E64"),sQuery(id+"F12.wireOp",EDGE,"E65"),sQuery(id+"F12.wireOp",EDGE,"E66"),sQuery(id+"F12.wireOp",EDGE,"E67"),sQuery(id+"F12.wireOp",EDGE,"E68"),sQuery(id+"F12.wireOp",EDGE,"E69"),sQuery(id+"F12.wireOp",EDGE,"E70"),sQuery(id+"F12.wireOp",EDGE,"E71"),sQuery(id+"F12.wireOp",EDGE,"E72"),sQuery(id+"F12.wireOp",EDGE,"E73"),sQuery(id+"F12.wireOp",EDGE,"E74"),sQuery(id+"F12.wireOp",EDGE,"E75"),sQuery(id+"F12.wireOp",EDGE,"E76"),sQuery(id+"F12.wireOp",EDGE,"E77"),sQuery(id+"F12.wireOp",EDGE,"E78"),sQuery(id+"F12.wireOp",EDGE,"E79"),sQuery(id+"F12.wireOp",EDGE,"E80"),sQuery(id+"F12.wireOp",EDGE,"E81"),sQuery(id+"F12.wireOp",EDGE,"E82")])],"isStart":false});
            extrude(context, id + "F14", {"entities" : qUnion([Q0]), "operationType" : NewBodyOperationType.REMOVE, "oppositeDirection" : true, "depth" : 10.16 * mm, "offsetDistance" : 25.4 * mm});
        }
        {
            var Q0;
            Q0=makeQuery(id+"F14.boolean.opBoolean","COPY",FACE,{"derivedFrom":makeQuery(id+"F14.opExtrude","CAP_FACE",FACE,{"disambiguationData":[OSD([sQuery(id+"F12.wireOp",EDGE,"E23"),sQuery(id+"F12.wireOp",EDGE,"E24"),sQuery(id+"F12.wireOp",EDGE,"E25"),sQuery(id+"F12.wireOp",EDGE,"E26"),sQuery(id+"F12.wireOp",EDGE,"E27"),sQuery(id+"F12.wireOp",EDGE,"E28"),sQuery(id+"F12.wireOp",EDGE,"E29"),sQuery(id+"F12.wireOp",EDGE,"E30"),sQuery(id+"F12.wireOp",EDGE,"E31"),sQuery(id+"F12.wireOp",EDGE,"E32"),sQuery(id+"F12.wireOp",EDGE,"E33"),sQuery(id+"F12.wireOp",EDGE,"E34"),sQuery(id+"F12.wireOp",EDGE,"E35"),sQuery(id+"F12.wireOp",EDGE,"E36"),sQuery(id+"F12.wireOp",EDGE,"E37"),sQuery(id+"F12.wireOp",EDGE,"E38"),sQuery(id+"F12.wireOp",EDGE,"E39"),sQuery(id+"F12.wireOp",EDGE,"E40"),sQuery(id+"F12.wireOp",EDGE,"E41"),sQuery(id+"F12.wireOp",EDGE,"E42"),sQuery(id+"F12.wireOp",EDGE,"E43"),sQuery(id+"F12.wireOp",EDGE,"E44"),sQuery(id+"F12.wireOp",EDGE,"E45"),sQuery(id+"F12.wireOp",EDGE,"E46"),sQuery(id+"F12.wireOp",EDGE,"E47"),sQuery(id+"F12.wireOp",EDGE,"E48"),sQuery(id+"F12.wireOp",EDGE,"E49"),sQuery(id+"F12.wireOp",EDGE,"E50"),sQuery(id+"F12.wireOp",EDGE,"E51"),sQuery(id+"F12.wireOp",EDGE,"E52"),sQuery(id+"F12.wireOp",EDGE,"E53"),sQuery(id+"F12.wireOp",EDGE,"E54"),sQuery(id+"F12.wireOp",EDGE,"E55"),sQuery(id+"F12.wireOp",EDGE,"E56"),sQuery(id+"F12.wireOp",EDGE,"E57"),sQuery(id+"F12.wireOp",EDGE,"E58"),sQuery(id+"F12.wireOp",EDGE,"E59"),sQuery(id+"F12.wireOp",EDGE,"E60"),sQuery(id+"F12.wireOp",EDGE,"E61"),sQuery(id+"F12.wireOp",EDGE,"E62"),sQuery(id+"F12.wireOp",EDGE,"E63"),sQuery(id+"F12.wireOp",EDGE,"E64"),sQuery(id+"F12.wireOp",EDGE,"E65"),sQuery(id+"F12.wireOp",EDGE,"E66"),sQuery(id+"F12.wireOp",EDGE,"E67"),sQuery(id+"F12.wireOp",EDGE,"E68"),sQuery(id+"F12.wireOp",EDGE,"E69"),sQuery(id+"F12.wireOp",EDGE,"E70"),sQuery(id+"F12.wireOp",EDGE,"E71"),sQuery(id+"F12.wireOp",EDGE,"E72"),sQuery(id+"F12.wireOp",EDGE,"E73"),sQuery(id+"F12.wireOp",EDGE,"E74"),sQuery(id+"F12.wireOp",EDGE,"E75"),sQuery(id+"F12.wireOp",EDGE,"E76"),sQuery(id+"F12.wireOp",EDGE,"E77"),sQuery(id+"F12.wireOp",EDGE,"E78"),sQuery(id+"F12.wireOp",EDGE,"E79"),sQuery(id+"F12.wireOp",EDGE,"E80"),sQuery(id+"F12.wireOp",EDGE,"E81"),sQuery(id+"F12.wireOp",EDGE,"E82")])],"isStart":false})});
            extrude(context, id + "F15", {"entities" : qUnion([Q0]), "operationType" : NewBodyOperationType.ADD, "oppositeDirection" : true, "depth" : 25.4 * mm, "offsetDistance" : 25.4 * mm});
        }
        {
            var Q0;
            Q0=makeQuery(id+"F15.opExtrude","CAP_FACE",FACE,{"disambiguationData":[OSD([sQuery(id+"F12.wireOp",EDGE,"E23"),sQuery(id+"F12.wireOp",EDGE,"E24"),sQuery(id+"F12.wireOp",EDGE,"E25"),sQuery(id+"F12.wireOp",EDGE,"E26"),sQuery(id+"F12.wireOp",EDGE,"E27"),sQuery(id+"F12.wireOp",EDGE,"E28"),sQuery(id+"F12.wireOp",EDGE,"E29"),sQuery(id+"F12.wireOp",EDGE,"E30"),sQuery(id+"F12.wireOp",EDGE,"E31"),sQuery(id+"F12.wireOp",EDGE,"E32"),sQuery(id+"F12.wireOp",EDGE,"E33"),sQuery(id+"F12.wireOp",EDGE,"E34"),sQuery(id+"F12.wireOp",EDGE,"E35"),sQuery(id+"F12.wireOp",EDGE,"E36"),sQuery(id+"F12.wireOp",EDGE,"E37"),sQuery(id+"F12.wireOp",EDGE,"E38"),sQuery(id+"F12.wireOp",EDGE,"E39"),sQuery(id+"F12.wireOp",EDGE,"E40"),sQuery(id+"F12.wireOp",EDGE,"E41"),sQuery(id+"F12.wireOp",EDGE,"E42"),sQuery(id+"F12.wireOp",EDGE,"E43"),sQuery(id+"F12.wireOp",EDGE,"E44"),sQuery(id+"F12.wireOp",EDGE,"E45"),sQuery(id+"F12.wireOp",EDGE,"E46"),sQuery(id+"F12.wireOp",EDGE,"E47"),sQuery(id+"F12.wireOp",EDGE,"E48"),sQuery(id+"F12.wireOp",EDGE,"E49"),sQuery(id+"F12.wireOp",EDGE,"E50"),sQuery(id+"F12.wireOp",EDGE,"E51"),sQuery(id+"F12.wireOp",EDGE,"E52"),sQuery(id+"F12.wireOp",EDGE,"E53"),sQuery(id+"F12.wireOp",EDGE,"E54"),sQuery(id+"F12.wireOp",EDGE,"E55"),sQuery(id+"F12.wireOp",EDGE,"E56"),sQuery(id+"F12.wireOp",EDGE,"E57"),sQuery(id+"F12.wireOp",EDGE,"E58"),sQuery(id+"F12.wireOp",EDGE,"E59"),sQuery(id+"F12.wireOp",EDGE,"E60"),sQuery(id+"F12.wireOp",EDGE,"E61"),sQuery(id+"F12.wireOp",EDGE,"E62"),sQuery(id+"F12.wireOp",EDGE,"E63"),sQuery(id+"F12.wireOp",EDGE,"E64"),sQuery(id+"F12.wireOp",EDGE,"E65"),sQuery(id+"F12.wireOp",EDGE,"E66"),sQuery(id+"F12.wireOp",EDGE,"E67"),sQuery(id+"F12.wireOp",EDGE,"E68"),sQuery(id+"F12.wireOp",EDGE,"E69"),sQuery(id+"F12.wireOp",EDGE,"E70"),sQuery(id+"F12.wireOp",EDGE,"E71"),sQuery(id+"F12.wireOp",EDGE,"E72"),sQuery(id+"F12.wireOp",EDGE,"E73"),sQuery(id+"F12.wireOp",EDGE,"E74"),sQuery(id+"F12.wireOp",EDGE,"E75"),sQuery(id+"F12.wireOp",EDGE,"E76"),sQuery(id+"F12.wireOp",EDGE,"E77"),sQuery(id+"F12.wireOp",EDGE,"E78"),sQuery(id+"F12.wireOp",EDGE,"E79"),sQuery(id+"F12.wireOp",EDGE,"E80"),sQuery(id+"F12.wireOp",EDGE,"E81"),sQuery(id+"F12.wireOp",EDGE,"E82")])],"isStart":false});
            extrude(context, id + "F16", {"entities" : qUnion([Q0]), "operationType" : NewBodyOperationType.REMOVE, "oppositeDirection" : true, "depth" : 6.35 * mm, "offsetDistance" : 25.4 * mm});
        }
        {
            var Q0;
            Q0=makeQuery(id+"F14.boolean.opBoolean","COPY",FACE,{"derivedFrom":makeQuery(id+"F14.opExtrude","CAP_FACE",FACE,{"disambiguationData":[OSD([sQuery(id+"F12.wireOp",EDGE,"E23"),sQuery(id+"F12.wireOp",EDGE,"E24"),sQuery(id+"F12.wireOp",EDGE,"E25"),sQuery(id+"F12.wireOp",EDGE,"E26"),sQuery(id+"F12.wireOp",EDGE,"E27"),sQuery(id+"F12.wireOp",EDGE,"E28"),sQuery(id+"F12.wireOp",EDGE,"E29"),sQuery(id+"F12.wireOp",EDGE,"E30"),sQuery(id+"F12.wireOp",EDGE,"E31"),sQuery(id+"F12.wireOp",EDGE,"E32"),sQuery(id+"F12.wireOp",EDGE,"E33"),sQuery(id+"F12.wireOp",EDGE,"E34"),sQuery(id+"F12.wireOp",EDGE,"E35"),sQuery(id+"F12.wireOp",EDGE,"E36"),sQuery(id+"F12.wireOp",EDGE,"E37"),sQuery(id+"F12.wireOp",EDGE,"E38"),sQuery(id+"F12.wireOp",EDGE,"E39"),sQuery(id+"F12.wireOp",EDGE,"E40"),sQuery(id+"F12.wireOp",EDGE,"E41"),sQuery(id+"F12.wireOp",EDGE,"E42"),sQuery(id+"F12.wireOp",EDGE,"E43"),sQuery(id+"F12.wireOp",EDGE,"E44"),sQuery(id+"F12.wireOp",EDGE,"E45"),sQuery(id+"F12.wireOp",EDGE,"E46"),sQuery(id+"F12.wireOp",EDGE,"E47"),sQuery(id+"F12.wireOp",EDGE,"E48"),sQuery(id+"F12.wireOp",EDGE,"E49"),sQuery(id+"F12.wireOp",EDGE,"E50"),sQuery(id+"F12.wireOp",EDGE,"E51"),sQuery(id+"F12.wireOp",EDGE,"E52"),sQuery(id+"F12.wireOp",EDGE,"E53"),sQuery(id+"F12.wireOp",EDGE,"E54"),sQuery(id+"F12.wireOp",EDGE,"E55"),sQuery(id+"F12.wireOp",EDGE,"E56"),sQuery(id+"F12.wireOp",EDGE,"E57"),sQuery(id+"F12.wireOp",EDGE,"E58"),sQuery(id+"F12.wireOp",EDGE,"E59"),sQuery(id+"F12.wireOp",EDGE,"E60"),sQuery(id+"F12.wireOp",EDGE,"E61"),sQuery(id+"F12.wireOp",EDGE,"E62"),sQuery(id+"F12.wireOp",EDGE,"E63"),sQuery(id+"F12.wireOp",EDGE,"E64"),sQuery(id+"F12.wireOp",EDGE,"E65"),sQuery(id+"F12.wireOp",EDGE,"E66"),sQuery(id+"F12.wireOp",EDGE,"E67"),sQuery(id+"F12.wireOp",EDGE,"E68"),sQuery(id+"F12.wireOp",EDGE,"E69"),sQuery(id+"F12.wireOp",EDGE,"E70"),sQuery(id+"F12.wireOp",EDGE,"E71"),sQuery(id+"F12.wireOp",EDGE,"E72"),sQuery(id+"F12.wireOp",EDGE,"E73"),sQuery(id+"F12.wireOp",EDGE,"E74"),sQuery(id+"F12.wireOp",EDGE,"E75"),sQuery(id+"F12.wireOp",EDGE,"E76"),sQuery(id+"F12.wireOp",EDGE,"E77"),sQuery(id+"F12.wireOp",EDGE,"E78"),sQuery(id+"F12.wireOp",EDGE,"E79"),sQuery(id+"F12.wireOp",EDGE,"E80"),sQuery(id+"F12.wireOp",EDGE,"E81"),sQuery(id+"F12.wireOp",EDGE,"E82")])],"isStart":false})});
            extrude(context, id + "F17", {"entities" : qUnion([Q0]), "operationType" : NewBodyOperationType.REMOVE, "oppositeDirection" : true, "depth" : 3.05 * mm, "offsetDistance" : 25.4 * mm});
        }
        {
            var Q0;
            Q0=makeQuery(id+"F17.boolean.opBoolean","COPY",FACE,{"derivedFrom":makeQuery(id+"F17.opExtrude","CAP_FACE",FACE,{"disambiguationData":[OSD([sQuery(id+"F12.wireOp",EDGE,"E23"),sQuery(id+"F12.wireOp",EDGE,"E24"),sQuery(id+"F12.wireOp",EDGE,"E25"),sQuery(id+"F12.wireOp",EDGE,"E26"),sQuery(id+"F12.wireOp",EDGE,"E27"),sQuery(id+"F12.wireOp",EDGE,"E28"),sQuery(id+"F12.wireOp",EDGE,"E29"),sQuery(id+"F12.wireOp",EDGE,"E30"),sQuery(id+"F12.wireOp",EDGE,"E31"),sQuery(id+"F12.wireOp",EDGE,"E32"),sQuery(id+"F12.wireOp",EDGE,"E33"),sQuery(id+"F12.wireOp",EDGE,"E34"),sQuery(id+"F12.wireOp",EDGE,"E35"),sQuery(id+"F12.wireOp",EDGE,"E36"),sQuery(id+"F12.wireOp",EDGE,"E37"),sQuery(id+"F12.wireOp",EDGE,"E38"),sQuery(id+"F12.wireOp",EDGE,"E39"),sQuery(id+"F12.wireOp",EDGE,"E40"),sQuery(id+"F12.wireOp",EDGE,"E41"),sQuery(id+"F12.wireOp",EDGE,"E42"),sQuery(id+"F12.wireOp",EDGE,"E43"),sQuery(id+"F12.wireOp",EDGE,"E44"),sQuery(id+"F12.wireOp",EDGE,"E45"),sQuery(id+"F12.wireOp",EDGE,"E46"),sQuery(id+"F12.wireOp",EDGE,"E47"),sQuery(id+"F12.wireOp",EDGE,"E48"),sQuery(id+"F12.wireOp",EDGE,"E49"),sQuery(id+"F12.wireOp",EDGE,"E50"),sQuery(id+"F12.wireOp",EDGE,"E51"),sQuery(id+"F12.wireOp",EDGE,"E52"),sQuery(id+"F12.wireOp",EDGE,"E53"),sQuery(id+"F12.wireOp",EDGE,"E54"),sQuery(id+"F12.wireOp",EDGE,"E55"),sQuery(id+"F12.wireOp",EDGE,"E56"),sQuery(id+"F12.wireOp",EDGE,"E57"),sQuery(id+"F12.wireOp",EDGE,"E58"),sQuery(id+"F12.wireOp",EDGE,"E59"),sQuery(id+"F12.wireOp",EDGE,"E60"),sQuery(id+"F12.wireOp",EDGE,"E61"),sQuery(id+"F12.wireOp",EDGE,"E62"),sQuery(id+"F12.wireOp",EDGE,"E63"),sQuery(id+"F12.wireOp",EDGE,"E64"),sQuery(id+"F12.wireOp",EDGE,"E65"),sQuery(id+"F12.wireOp",EDGE,"E66"),sQuery(id+"F12.wireOp",EDGE,"E67"),sQuery(id+"F12.wireOp",EDGE,"E68"),sQuery(id+"F12.wireOp",EDGE,"E69"),sQuery(id+"F12.wireOp",EDGE,"E70"),sQuery(id+"F12.wireOp",EDGE,"E71"),sQuery(id+"F12.wireOp",EDGE,"E72"),sQuery(id+"F12.wireOp",EDGE,"E73"),sQuery(id+"F12.wireOp",EDGE,"E74"),sQuery(id+"F12.wireOp",EDGE,"E75"),sQuery(id+"F12.wireOp",EDGE,"E76"),sQuery(id+"F12.wireOp",EDGE,"E77"),sQuery(id+"F12.wireOp",EDGE,"E78"),sQuery(id+"F12.wireOp",EDGE,"E79"),sQuery(id+"F12.wireOp",EDGE,"E80"),sQuery(id+"F12.wireOp",EDGE,"E81"),sQuery(id+"F12.wireOp",EDGE,"E82")])],"isStart":false})});
            extrude(context, id + "F18", {"entities" : qUnion([Q0]), "operationType" : NewBodyOperationType.REMOVE, "oppositeDirection" : true, "depth" : 0.25 * mm, "offsetDistance" : 25.4 * mm});
        }
        {
            var Q0;
            Q0=qCreatedBy(makeId("Top.planeOp"),FACE);
            var sketch = newSketch(context, id + "F19", { "sketchPlane" : qUnion([Q0])});
            skLineSegment(sketch, "E83.bottom", {"start": v(-113.99, 82.2) * mm, "end": v(116.2, 82.2) * mm});
            skLineSegment(sketch, "E83.top", {"start": v(-113.99, -87.1) * mm, "end": v(116.2, -87.1) * mm});
            skLineSegment(sketch, "E83.left", {"start": v(-113.99, 82.2) * mm, "end": v(-113.99, -87.1) * mm});
            skLineSegment(sketch, "E83.right", {"start": v(116.2, 82.2) * mm, "end": v(116.2, -87.1) * mm});
            skSolve(sketch);
        }
        {
            var Q0;
            Q0=makeQuery(id+"F19.imprint","IMPRINT",FACE,{"disambiguationData":[TD([[makeQuery(id+"F19.imprint","IMPRINT",EDGE,{"derivedFrom":sQuery(id+"F19.wireOp",EDGE,"E83.bottom")}),-1.0]])]});
            extrude(context, id + "F20", {"entities" : qUnion([Q0]), "operationType" : NewBodyOperationType.ADD, "depth" : 756.72 * mm, "offsetDistance" : 25.4 * mm, "hasSecondDirection" : true, "secondDirectionOppositeDirection" : false, "secondDirectionDepth" : 519.84 * mm});
        }
        {
            var Q0;
            Q0=qCreatedBy(makeId("Front.planeOp"),FACE);
            var sketch = newSketch(context, id + "F21", { "sketchPlane" : qUnion([Q0])});
            skLineSegment(sketch, "E84", {"start": v(-113.25, 520.88) * mm, "end": v(-216.07, 755.15) * mm});
            skLineSegment(sketch, "E85", {"start": v(-216.07, 755.15) * mm, "end": v(-216.07, 755.15) * mm});
            skLineSegment(sketch, "E86", {"start": v(-216.07, 755.15) * mm, "end": v(-112.38, 755.15) * mm});
            skLineSegment(sketch, "E87", {"start": v(-112.38, 755.15) * mm, "end": v(-113.25, 520.88) * mm});
            skLineSegment(sketch, "E88.MirrorCS", {"start": v(112.38, 755.15) * mm, "end": v(113.25, 520.88) * mm});
            skLineSegment(sketch, "E89.MirrorCS", {"start": v(113.25, 520.88) * mm, "end": v(216.07, 755.15) * mm});
            skLineSegment(sketch, "E90.MirrorCS", {"start": v(216.07, 755.15) * mm, "end": v(112.38, 755.15) * mm});
            skSolve(sketch);
        }
        {
            var Q0;
            Q0=makeQuery(id+"F21.imprint","IMPRINT",FACE,{"disambiguationData":[TD([[makeQuery(id+"F21.imprint","IMPRINT",EDGE,{"derivedFrom":sQuery(id+"F21.wireOp",EDGE,"E88.MirrorCS")}),1.0]])]});
            var Q1;
            Q1=makeQuery(id+"F21.imprint","IMPRINT",FACE,{"disambiguationData":[TD([[makeQuery(id+"F21.imprint","IMPRINT",EDGE,{"derivedFrom":sQuery(id+"F21.wireOp",EDGE,"E84")}),-1.0]])]});
            extrude(context, id + "F22", {"entities" : qUnion([Q0, Q1]), "operationType" : NewBodyOperationType.ADD, "depth" : 90.05 * mm, "offsetDistance" : 25.4 * mm, "hasSecondDirection" : true, "secondDirectionOppositeDirection" : true, "secondDirectionDepth" : 80.58 * mm});
        }
    });
